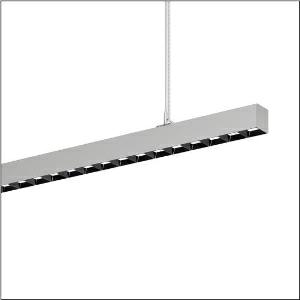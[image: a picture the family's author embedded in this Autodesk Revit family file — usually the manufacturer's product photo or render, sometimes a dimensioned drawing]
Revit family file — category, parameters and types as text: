
# Revit family: silica_r__21_51mx31dc4dsb_9913
name_source: partatom
category: Lighting Fixtures
units: mm (PartAtom-declared; Revit-internal decimal feet)

## family parameters
Cut with Voids When Loaded = No
Host = Face
Light Source = No
Part Type = Normal
Room Calculation Point = No
Round Connector Dimension = Use Diameter
Shared = No

## types (1)
- --- (1 x LED, 18230 lm, 105.9 W, 4000K)
    Apparent Load = 106 VA
    CIE Flux Codes = 87 99 100 59 100
    Color Rendering = 80
    Color Temperature = 4000K
    Default Elevation = 1800 mm
    Description = Silica® 21, office luminaire, primary light control with darklight reflector, of PMMA, black, CAT 2 (L<= 3000cd/m²), light emission: direct/indirect distribution, primary light characteristic: symmetric, installation type: suspended mounting, LED, rated luminous flux: 18.230lm, luminous efficacy: 172lm/W, light colour: 840, colour temperature: 4000K, with terminal, 3+2-pole, max. 2.5mm², mains connection: 220..240V, AC, 50/60Hz, rated input power: 105.9W, luminaire housing, of aluminium, metallic grey (RAL 9006), length: 3.004mm, width: 53mm, height: 53mm, protection rating (complete): IP20, insulation class (complete): insulation class I (protective earthing), certification: CE, permissible operating ambient temperature: 0..+35°C, standard: EN 50419, packaging unit: 1 piece
    Height = 53 mm
    Lamp = 1 x LED
    Lamp Light Flux = 18230 lm
    Lamp Power = 105.9 W
    Lamp count = 1
    Length = 3004 mm
    Luminous efficacy = 172 lm/W
    Manufacturer = Siteco
    ModVariant = No
    Model = 51MX31DC4DSB
    Mounting Place = Ceiling
    Mounting Type = Pendant
    Number of Poles = 1
    OnlyDefault = Yes
    Power Factor = 1
    Product Name = Silica® 21
    Product group = office luminaire | ceiling pendant
    ProductGroupID = 902
    Protection Class = Protection class I
    Protection Degree = IP 20
    RLX_Detail_Level = 1
    RLX_Emergency_Light_Flux = 0 lm
    RLX_Emergency_Type = 0
    RLX_Emergency_Type_DB = No
    RlxData = <blob elided: 65533 chars, md5=79a7c267>
    Socket = socket
    Standby Power = 0 W
    System Light Flux = 18230 lm
    System Power = 106 W
    Type Comments = factory setting: luminous flux: 100 % | dim-lin: 254 | 367 mA
    Type Image = l_1313642.jpg
    URL = http://relux.com
    VarID = @adj_069829
    Voltage = 0 V
    Weight = 0.00 kg
    Width = 53 mm

## geometry (parser evidence)
native form markers: Blend x4, Sweep x13
no freeform markers — native parametric forms only
